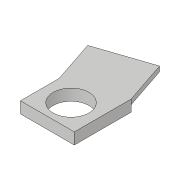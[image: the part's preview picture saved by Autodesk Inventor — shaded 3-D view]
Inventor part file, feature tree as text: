
AUTODESK INVENTOR PART (.ipt)
format: ipt  version: 2018.3 (Build 223284000, 284)  size: 119,296 bytes
history: native  units: in
note: dims shown in document units (in); Inventor stores cm internally (conversion verified against a paired STEP export)
features: extrude x2, sketch x1
ambient origin geometry x8: Origin, YZ Plane, XZ Plane, XY Plane, X Axis, Y Axis, Z Axis, Center Point
bodies: Solid1 (feature_tree)
feature tree (3):
  extrude  "Extrusion1"  Depth=0.1105in
  extrude  "Extrusion2"  Depth=1.1003in
  sketch  "Sketch1"  dims[d0=0.75in d1=0.875in d2=1.1003in d3=1.0432in d4=0.6925in d5=0.221in d6=0.0in d7=0.125in d8=0.0in d18=0.5216in d20=1.1095in d24=0.1105in d26=0.4588in d27=0.119in]
